# Revit family: Gaius Senior Basin_
name_source: partatom
category: Plumbing Fixtures
revit_build: Autodesk Revit Architecture 2012 (Build: 20110916_2132(x64)
units: mm (PartAtom-declared; Revit-internal decimal feet)

## types (26) — shared parameters
Height = 800 mm  [stored 2.62467 ft]
Vent Connection = No
allas = Cast Marble - White

## per-type parameters (varying)
| type | Drain Pipe Material | Kannakkeet | L | Nostin | R | kaide |
| 6401 | Chrome - Polished | Yes | 300 mm  [stored 0.984252 ft] | No | 300 mm  [stored 0.984252 ft] | RAL 9016 - White |
| 6401K | Chrome - Polished | Yes | 300 mm  [stored 0.984252 ft] | No | 300 mm  [stored 0.984252 ft] | RAL 1004 - Yellow |
| 6401H | <By Category> | Yes | 300 mm  [stored 0.984252 ft] | No | 300 mm  [stored 0.984252 ft] | RAL 7037 - Grey |
| 6401P | Chrome - Polished | Yes | 300 mm  [stored 0.984252 ft] | No | 300 mm  [stored 0.984252 ft] | RAL 3003 - Red |
| 6402 | Chrome - Polished | Yes | 600 mm  [stored 1.9685 ft] | No | 300 mm  [stored 0.984252 ft] | RAL 9016 - White |
| 6402K | Chrome - Polished | Yes | 600 mm  [stored 1.9685 ft] | No | 300 mm  [stored 0.984252 ft] | RAL 1004 - Yellow |
| 6402H | Chrome - Polished | Yes | 600 mm  [stored 1.9685 ft] | No | 300 mm  [stored 0.984252 ft] | RAL 7037 - Grey |
| 6402P | Chrome - Polished | Yes | 600 mm  [stored 1.9685 ft] | No | 300 mm  [stored 0.984252 ft] | RAL 3003 - Red |
| 6403P | Chrome - Polished | Yes | 300 mm  [stored 0.984252 ft] | No | 600 mm  [stored 1.9685 ft] | RAL 3003 - Red |
| 6403H | Chrome - Polished | Yes | 300 mm  [stored 0.984252 ft] | No | 600 mm  [stored 1.9685 ft] | RAL 7037 - Grey |
| 6403K | Chrome - Polished | Yes | 300 mm  [stored 0.984252 ft] | No | 600 mm  [stored 1.9685 ft] | RAL 1004 - Yellow |
| 6403 | Chrome - Polished | Yes | 300 mm  [stored 0.984252 ft] | No | 600 mm  [stored 1.9685 ft] | RAL 9016 - White |
| 6404 | Chrome - Polished | Yes | 600 mm  [stored 1.9685 ft] | No | 600 mm  [stored 1.9685 ft] | RAL 9016 - White |
| 6404 + 6238 | Chrome - Polished | No | 600 mm  [stored 1.9685 ft] | Yes | 600 mm  [stored 1.9685 ft] | RAL 9016 - White |
| 6403P + 6238 | Chrome - Polished | No | 300 mm  [stored 0.984252 ft] | Yes | 600 mm  [stored 1.9685 ft] | RAL 3003 - Red |
| 6403K + 6238 | Chrome - Polished | No | 300 mm  [stored 0.984252 ft] | Yes | 600 mm  [stored 1.9685 ft] | RAL 1004 - Yellow |
| 6403H + 6238 | Chrome - Polished | No | 300 mm  [stored 0.984252 ft] | Yes | 600 mm  [stored 1.9685 ft] | RAL 7037 - Grey |
| 6403 + 6238 | Chrome - Polished | No | 300 mm  [stored 0.984252 ft] | Yes | 600 mm  [stored 1.9685 ft] | RAL 9016 - White |
| 6402P + 6238 | Chrome - Polished | No | 600 mm  [stored 1.9685 ft] | Yes | 300 mm  [stored 0.984252 ft] | RAL 3003 - Red |
| 6402K + 6238 | Chrome - Polished | No | 600 mm  [stored 1.9685 ft] | Yes | 300 mm  [stored 0.984252 ft] | RAL 1004 - Yellow |
| 6402H + 6238 | Chrome - Polished | No | 600 mm  [stored 1.9685 ft] | Yes | 300 mm  [stored 0.984252 ft] | RAL 7037 - Grey |
| 6402 + 6238 | Chrome - Polished | No | 600 mm  [stored 1.9685 ft] | Yes | 300 mm  [stored 0.984252 ft] | RAL 9016 - White |
| 6401P + 6238 | Chrome - Polished | No | 300 mm  [stored 0.984252 ft] | Yes | 300 mm  [stored 0.984252 ft] | RAL 3003 - Red |
| 6401K + 6238 | Chrome - Polished | No | 300 mm  [stored 0.984252 ft] | Yes | 300 mm  [stored 0.984252 ft] | RAL 1004 - Yellow |
| 6401H + 6238 | Chrome - Polished | No | 300 mm  [stored 0.984252 ft] | Yes | 300 mm  [stored 0.984252 ft] | RAL 7037 - Grey |
| 6401 + 6238 | Chrome - Polished | No | 300 mm  [stored 0.984252 ft] | Yes | 300 mm  [stored 0.984252 ft] | RAL 9016 - White |

note: [stored X ft] marks values corroborated as IEEE doubles in the binary element streams (Revit-internal decimal feet)

## geometry (parser evidence)
native form markers: Sweep x18
no freeform markers — native parametric forms only
